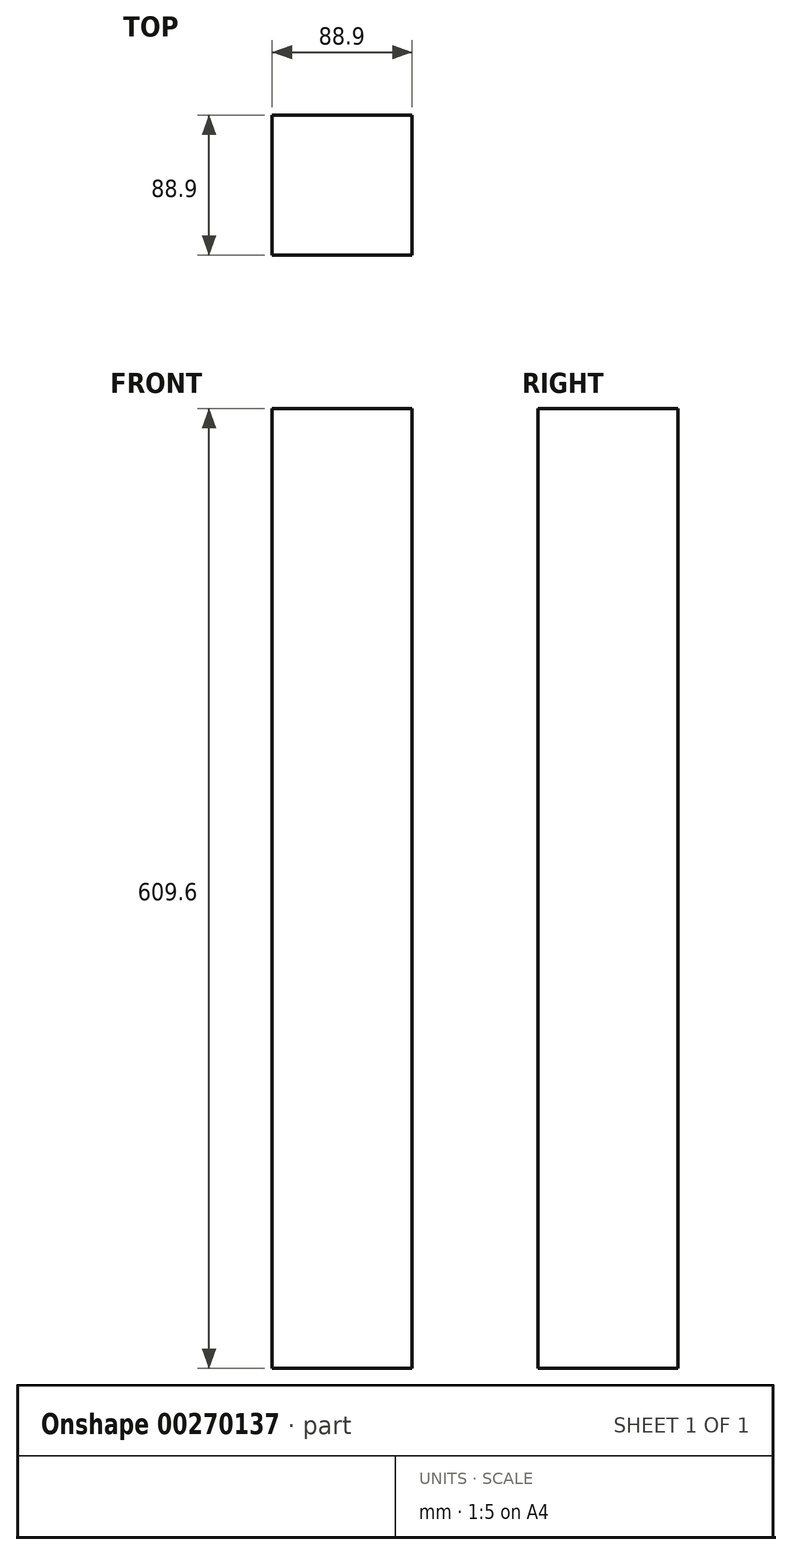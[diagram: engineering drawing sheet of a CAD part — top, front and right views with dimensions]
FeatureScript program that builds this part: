
annotation { "Feature Type Name" : "Feature", "Feature Type Description" : "" }
export const myFeature = defineFeature(function(context is Context, id is Id, definition is map)
    precondition{}
    {
        {
            var Q0;
            Q0=qCreatedBy(makeId("Top.planeOp"),FACE);
            var sketch = newSketch(context, id + "F0", { "sketchPlane" : qUnion([Q0])});
            skLineSegment(sketch, "E0.bottom", {"start": v(44.45, -44.45) * mm, "end": v(-44.45, -44.45) * mm});
            skLineSegment(sketch, "E0.top", {"start": v(44.45, 44.45) * mm, "end": v(-44.45, 44.45) * mm});
            skLineSegment(sketch, "E0.left", {"start": v(44.45, -44.45) * mm, "end": v(44.45, 44.45) * mm});
            skLineSegment(sketch, "E0.right", {"start": v(-44.45, -44.45) * mm, "end": v(-44.45, 44.45) * mm});
            skPoint(sketch, "E0.middle", {"position": v(0, 0) * mm});
            skSolve(sketch);
        }
        {
            var Q0;
            Q0=makeQuery(id+"F0.imprint","IMPRINT",FACE,{"disambiguationData":[TD([[makeQuery(id+"F0.imprint","IMPRINT",EDGE,{"derivedFrom":sQuery(id+"F0.wireOp",EDGE,"E0.bottom")}),-1.0]])]});
            extrude(context, id + "F1", {"entities" : qUnion([Q0]), "depth" : 609.6 * mm});
        }
    });
